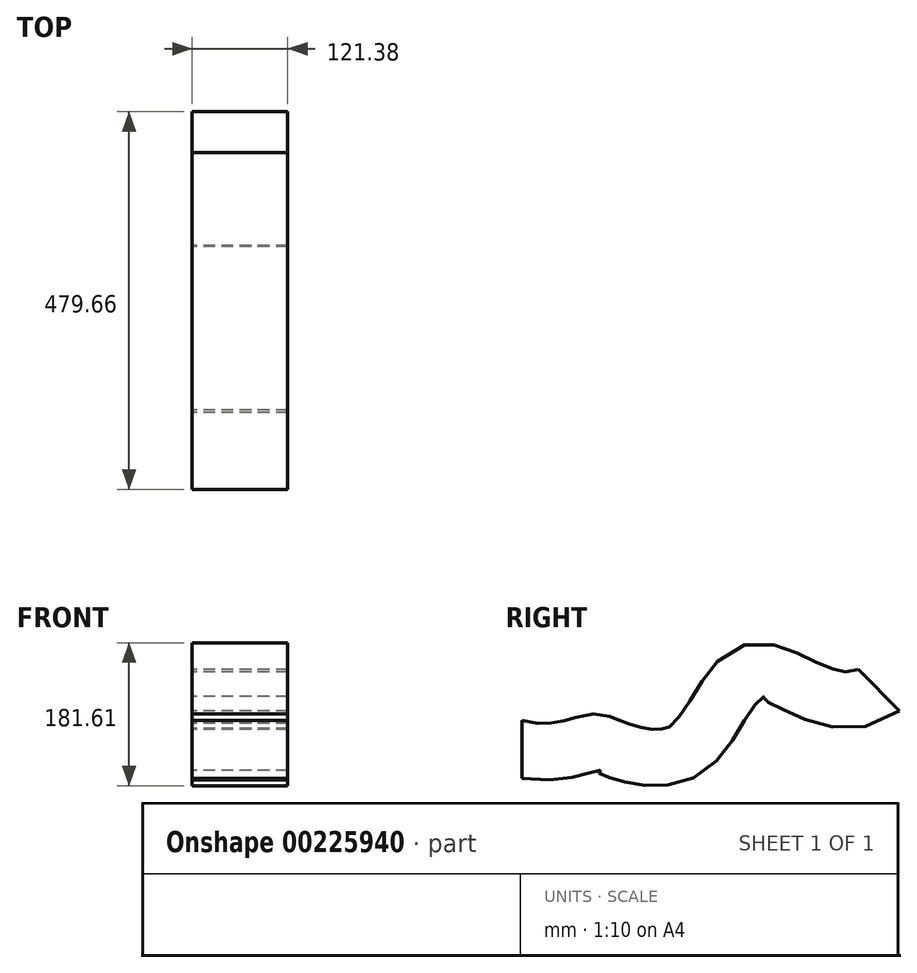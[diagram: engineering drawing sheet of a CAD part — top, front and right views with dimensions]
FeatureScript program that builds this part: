
annotation { "Feature Type Name" : "Feature", "Feature Type Description" : "" }
export const myFeature = defineFeature(function(context is Context, id is Id, definition is map)
    precondition{}
    {
        {
            var Q0;
            Q0=qCreatedBy(makeId("Front.planeOp"),FACE);
            var sketch = newSketch(context, id + "F0", { "sketchPlane" : qUnion([Q0])});
            skLineSegment(sketch, "E0.bottom", {"start": v(60.7, 36.82) * mm, "end": v(-60.7, 36.82) * mm});
            skLineSegment(sketch, "E0.top", {"start": v(60.7, -36.82) * mm, "end": v(-60.7, -36.82) * mm});
            skLineSegment(sketch, "E0.left", {"start": v(60.7, 36.82) * mm, "end": v(60.7, -36.82) * mm});
            skLineSegment(sketch, "E0.right", {"start": v(-60.7, 36.82) * mm, "end": v(-60.7, -36.82) * mm});
            skPoint(sketch, "E0.middle", {"position": v(0, 0) * mm});
            skSolve(sketch);
        }
        {
            var Q0;
            Q0=qCreatedBy(makeId("Right.planeOp"),FACE);
            var sketch = newSketch(context, id + "F1", { "sketchPlane" : qUnion([Q0])});
            skFitSpline(sketch, "E1", {"points": [v(0, -0.94) * mm, v(90.5, 7.15) * mm, v(116.16, 0) * mm, v(210.26, 0) * mm, v(296.05, 97.34) * mm, v(454.42, 74.38) * mm], "startDerivative": vector(704.73, -143.72) * mm, "endDerivative": vector(701.15, 458.66) * mm});
            skSolve(sketch);
        }
        {
            var Q0;
            Q0=makeQuery(id+"F0.imprint","IMPRINT",FACE,{"disambiguationData":[TD([[makeQuery(id+"F0.imprint","IMPRINT",EDGE,{"derivedFrom":sQuery(id+"F0.wireOp",EDGE,"E0.bottom")}),1.0]])]});
            var Q1;
            Q1=sQuery(id+"F1.wireOp",EDGE,"E1");
            sweep(context, id + "F2", {"profiles" : qUnion([Q0]), "path" : qUnion([Q1])});
        }
    });
